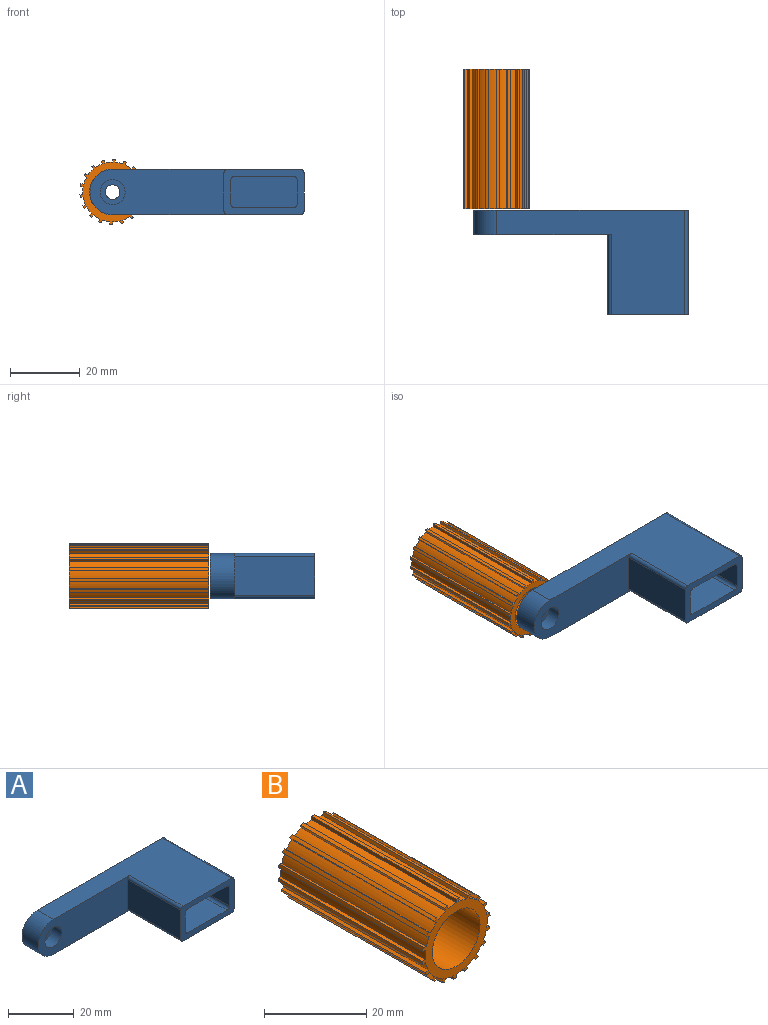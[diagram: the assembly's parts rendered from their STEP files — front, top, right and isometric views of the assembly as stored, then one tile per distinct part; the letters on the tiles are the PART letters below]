
ASSEMBLY  parts=2 mates=1
PART A: 24 faces, bbox 61.5x30x13 mm
  f0: plane 61.5x13mm, normal (0,1,0), area 767.1mm2, adj f2,f3,f4,f5,f8,f9,f21
  f1: plane 39.5x13mm, normal (0,-1,0), area 442.1mm2, adj f2,f3,f5,f6,f10,f11,f12
  f2: plane 54x30mm, normal (0,0,-1), area 861mm2, adj f0,f1,f5,f12,f21,f22
  f3: plane 54x30mm, normal (0,0,1), area 861mm2, adj f0,f1,f5,f9,f10,f22
  f4: cylinder r=2.1mm len=4.2mm, axis (0,-1,0), area 39.6mm2, adj f0,f7
  f5: cylinder r=6.5mm len=13mm, axis (0,-1,0), area 142.9mm2, adj f0,f1,f2,f3
  f6: cylinder r=3.6mm len=7.2mm, axis (0,-1,0), area 90.5mm2, adj f1,f7
  f7: plane 7.2x7.2mm, normal (0,-1,0), area 26.9mm2, adj f4,f6
  f8: plane 30x11mm, normal (1,0,0), area 330mm2, adj f0,f9,f21,f22
  f9: cylinder r=1mm len=30mm, axis (0,1,0), area 47.1mm2, adj f0,f3,f8,f22
  f10: cylinder r=1mm len=23mm, axis (0,1,0), area 36.1mm2, adj f1,f3,f11,f22
  f11: plane 23x11mm, normal (-1,0,0), area 253mm2, adj f1,f10,f12,f22
  f12: cylinder r=1mm len=23mm, axis (0,1,0), area 36.1mm2, adj f1,f2,f11,f22
  f13: cylinder r=1mm len=17mm, axis (0,1,0), area 26.7mm2, adj f14,f20,f22,f23
  f14: plane 17x17mm, normal (0,0,-1), area 289mm2, adj f13,f15,f22,f23
  f15: cylinder r=1mm len=17mm, axis (0,1,0), area 26.7mm2, adj f14,f16,f22,f23
  f16: plane 17x7mm, normal (-1,0,0), area 119mm2, adj f15,f17,f22,f23
  f17: cylinder r=1mm len=17mm, axis (0,1,0), area 26.7mm2, adj f16,f18,f22,f23
  f18: plane 17x17mm, normal (0,0,1), area 289mm2, adj f17,f19,f22,f23
  f19: cylinder r=1mm len=17mm, axis (0,1,0), area 26.7mm2, adj f18,f20,f22,f23
  f20: plane 17x7mm, normal (1,0,0), area 119mm2, adj f13,f19,f22,f23
  f21: cylinder r=1mm len=30mm, axis (0,1,0), area 47.1mm2, adj f0,f2,f8,f22
  f22: plane 23x13mm, normal (0,-1,0), area 128mm2, adj f2,f3,f8,f9,f10,f11,f12,f13
  f23: plane 19x9mm, normal (0,-1,0), area 170.1mm2, adj f13,f14,f15,f16,f17,f18,f19,f20
PART B: 83 faces, bbox 18.7x40x18.8 mm
  f0: cylinder r=6.6mm len=19mm, axis (0,1,0), area 787.9mm2, adj f78,f82
  f1: cylinder r=6.6mm len=13.2mm, axis (0,1,0), area 497.6mm2, adj f75,f81
  f2: plane 40x0.69mm, normal (-0.5,0,-0.87), area 32mm2, adj f3,f74,f75,f76
  f3: cylinder r=8.6mm len=40mm, axis (0,1,0), area 90.1mm2, adj f2,f4,f75,f76
  f4: plane 40x0.77mm, normal (0.26,0,0.97), area 32mm2, adj f3,f5,f75,f76
  f5: cylinder r=9.4mm len=40mm, axis (0,1,0), area 32.8mm2, adj f4,f6,f75,f76
  f6: plane 40x0.79mm, normal (-0.17,0,-0.98), area 32mm2, adj f5,f7,f75,f76
  f7: cylinder r=8.6mm len=40mm, axis (0,1,0), area 90.1mm2, adj f6,f8,f75,f76
  f8: plane 40x0.8mm, normal (-0.09,0,1), area 32mm2, adj f7,f9,f75,f76
  f9: cylinder r=9.4mm len=40mm, axis (0,1,0), area 32.8mm2, adj f8,f10,f75,f76
  f10: plane 40x0.79mm, normal (0.17,0,-0.98), area 32mm2, adj f9,f11,f75,f76
  f11: cylinder r=8.6mm len=40mm, axis (0,1,0), area 90.1mm2, adj f10,f12,f75,f76
  f12: plane 40x0.73mm, normal (-0.42,0,0.91), area 32mm2, adj f11,f13,f75,f76
  f13: cylinder r=9.4mm len=40mm, axis (0,1,0), area 32.8mm2, adj f12,f14,f75,f76
  f14: plane 40x0.69mm, normal (0.5,0,-0.87), area 32mm2, adj f13,f15,f75,f76
  f15: cylinder r=8.6mm len=40mm, axis (0,1,0), area 90.1mm2, adj f14,f16,f75,f76
  f16: plane 40x0.57mm, normal (-0.71,0,0.71), area 32mm2, adj f15,f17,f75,f76
  f17: cylinder r=9.4mm len=40mm, axis (0,1,0), area 32.8mm2, adj f16,f18,f75,f76
  f18: plane 40x0.61mm, normal (0.77,0,-0.64), area 32mm2, adj f17,f19,f75,f76
  f19: cylinder r=8.6mm len=40mm, axis (0,1,0), area 90.1mm2, adj f18,f20,f75,f76
  f20: plane 40x0.73mm, normal (-0.91,0,0.42), area 32mm2, adj f19,f21,f75,f76
  f21: cylinder r=9.4mm len=40mm, axis (0,1,0), area 32.8mm2, adj f20,f22,f75,f76
  f22: plane 40x0.75mm, normal (0.94,0,-0.34), area 32mm2, adj f21,f23,f75,f76
  f23: cylinder r=8.6mm len=40mm, axis (0,1,0), area 90.1mm2, adj f22,f24,f75,f76
  f24: plane 40x0.8mm, normal (-1,0,0.09), area 32mm2, adj f23,f25,f75,f76
  f25: cylinder r=9.4mm len=40mm, axis (0,1,0), area 32.8mm2, adj f24,f26,f75,f76
  f26: plane 40x0.8mm, normal (1,0,0), area 32mm2, adj f25,f27,f75,f76
  f27: cylinder r=8.6mm len=40mm, axis (0,1,0), area 90.1mm2, adj f26,f28,f75,f76
  f28: plane 40x0.77mm, normal (-0.97,0,-0.26), area 32mm2, adj f27,f29,f75,f76
  f29: cylinder r=9.4mm len=40mm, axis (0,1,0), area 32.8mm2, adj f28,f30,f75,f76
  f30: plane 40x0.75mm, normal (0.94,0,0.34), area 32mm2, adj f29,f31,f75,f76
  f31: cylinder r=8.6mm len=40mm, axis (0,1,0), area 90.1mm2, adj f30,f32,f75,f76
  f32: plane 40x0.66mm, normal (-0.82,0,-0.57), area 32mm2, adj f31,f33,f75,f76
  f33: cylinder r=9.4mm len=40mm, axis (0,1,0), area 32.8mm2, adj f32,f34,f75,f76
  f34: plane 40x0.61mm, normal (0.77,0,0.64), area 32mm2, adj f33,f35,f75,f76
  f35: cylinder r=8.6mm len=40mm, axis (0,1,0), area 90.1mm2, adj f34,f36,f75,f76
  f36: plane 40x0.66mm, normal (-0.57,0,-0.82), area 32mm2, adj f35,f37,f75,f76
  f37: cylinder r=9.4mm len=40mm, axis (0,1,0), area 32.8mm2, adj f36,f38,f75,f76
  f38: plane 40x0.69mm, normal (0.5,0,0.87), area 32mm2, adj f37,f39,f75,f76
  f39: cylinder r=8.6mm len=40mm, axis (0,1,0), area 90.1mm2, adj f38,f40,f75,f76
  f40: plane 40x0.77mm, normal (-0.26,0,-0.97), area 32mm2, adj f39,f41,f75,f76
  f41: cylinder r=9.4mm len=40mm, axis (0,1,0), area 32.8mm2, adj f40,f42,f75,f76
  f42: plane 40x0.79mm, normal (0.17,0,0.98), area 32mm2, adj f41,f43,f75,f76
  f43: cylinder r=8.6mm len=40mm, axis (0,1,0), area 90.1mm2, adj f42,f44,f75,f76
  f44: plane 40x0.8mm, normal (0.09,0,-1), area 32mm2, adj f43,f45,f75,f76
  f45: cylinder r=9.4mm len=40mm, axis (0,1,0), area 32.8mm2, adj f44,f46,f75,f76
  f46: plane 40x0.79mm, normal (-0.17,0,0.98), area 32mm2, adj f45,f47,f75,f76
  f47: cylinder r=8.6mm len=40mm, axis (0,1,0), area 90.1mm2, adj f46,f48,f75,f76
  f48: plane 40x0.73mm, normal (0.42,0,-0.91), area 32mm2, adj f47,f49,f75,f76
  f49: cylinder r=9.4mm len=40mm, axis (0,1,0), area 32.8mm2, adj f48,f50,f75,f76
  f50: plane 40x0.69mm, normal (-0.5,0,0.87), area 32mm2, adj f49,f51,f75,f76
  f51: cylinder r=8.6mm len=40mm, axis (0,1,0), area 90.1mm2, adj f50,f52,f75,f76
  f52: plane 40x0.57mm, normal (0.71,0,-0.71), area 32mm2, adj f51,f53,f75,f76
  f53: cylinder r=9.4mm len=40mm, axis (0,1,0), area 32.8mm2, adj f52,f54,f75,f76
  f54: plane 40x0.61mm, normal (-0.77,0,0.64), area 32mm2, adj f53,f55,f75,f76
  f55: cylinder r=8.6mm len=40mm, axis (0,1,0), area 90.1mm2, adj f54,f56,f75,f76
  f56: plane 40x0.73mm, normal (0.91,0,-0.42), area 32mm2, adj f55,f57,f75,f76
  f57: cylinder r=9.4mm len=40mm, axis (0,1,0), area 32.8mm2, adj f56,f58,f75,f76
  f58: plane 40x0.75mm, normal (-0.94,0,0.34), area 32mm2, adj f57,f59,f75,f76
  f59: cylinder r=8.6mm len=40mm, axis (0,1,0), area 90.1mm2, adj f58,f60,f75,f76
  f60: plane 40x0.8mm, normal (1,0,-0.09), area 32mm2, adj f59,f61,f75,f76
  f61: cylinder r=9.4mm len=40mm, axis (0,1,0), area 32.8mm2, adj f60,f62,f75,f76
  f62: plane 40x0.8mm, normal (-1,0,0), area 32mm2, adj f61,f63,f75,f76
  f63: cylinder r=8.6mm len=40mm, axis (0,1,0), area 90.1mm2, adj f62,f64,f75,f76
  f64: plane 40x0.77mm, normal (0.97,0,0.26), area 32mm2, adj f63,f65,f75,f76
  f65: cylinder r=9.4mm len=40mm, axis (0,1,0), area 32.8mm2, adj f64,f66,f75,f76
  f66: plane 40x0.75mm, normal (-0.94,0,-0.34), area 32mm2, adj f65,f67,f75,f76
  f67: cylinder r=8.6mm len=40mm, axis (0,1,0), area 90.1mm2, adj f66,f68,f75,f76
  f68: plane 40x0.66mm, normal (0.82,0,0.57), area 32mm2, adj f67,f69,f75,f76
  f69: cylinder r=9.4mm len=40mm, axis (0,1,0), area 32.8mm2, adj f68,f70,f75,f76
  f70: plane 40x0.61mm, normal (-0.77,0,-0.64), area 32mm2, adj f69,f71,f75,f76
  f71: cylinder r=8.6mm len=40mm, axis (0,1,0), area 90.1mm2, adj f70,f72,f75,f76
  f72: plane 40x0.66mm, normal (0.57,0,0.82), area 32mm2, adj f71,f74,f75,f76
  f73: cylinder r=6.6mm len=13.2mm, axis (0,1,0), area 207.3mm2, adj f76,f79
  f74: cylinder r=9.4mm len=40mm, axis (0,1,0), area 32.8mm2, adj f2,f72,f75,f76
  f75: plane 18.8x18.73mm, normal (0,-1,0), area 106.8mm2, adj f1,f2,f3,f4,f5,f6,f7,f8
  f76: plane 18.8x18.73mm, normal (0,1,0), area 106.8mm2, adj f2,f3,f4,f5,f6,f7,f8,f9
  f77: cylinder r=5.6mm len=11.2mm, axis (0,1,0), area 35.2mm2, adj f78,f79
  f78: plane 13.2x13.2mm, normal (0,-1,0), area 38.3mm2, adj f0,f77
  f79: cone r=5.6mm half-angle=45deg, axis (0,1,0), area 54.2mm2, adj f73,f77
  f80: cylinder r=5.6mm len=11.2mm, axis (0,-1,0), area 35.2mm2, adj f81,f82
  f81: plane 13.2x13.2mm, normal (0,-1,0), area 38.3mm2, adj f1,f80
  f82: cone r=6.6mm half-angle=45deg, axis (0,1,0), area 54.2mm2, adj f0,f80
PLACE A t=(-3.85,-55.67,-10.18)mm
PLACE B t=(-47.35,-28.17,-10.18)mm
MATE revolute A.f4 <-> B.f0  axis (0,-1,0) through (-47.35,-48.67,-10.18)mm
